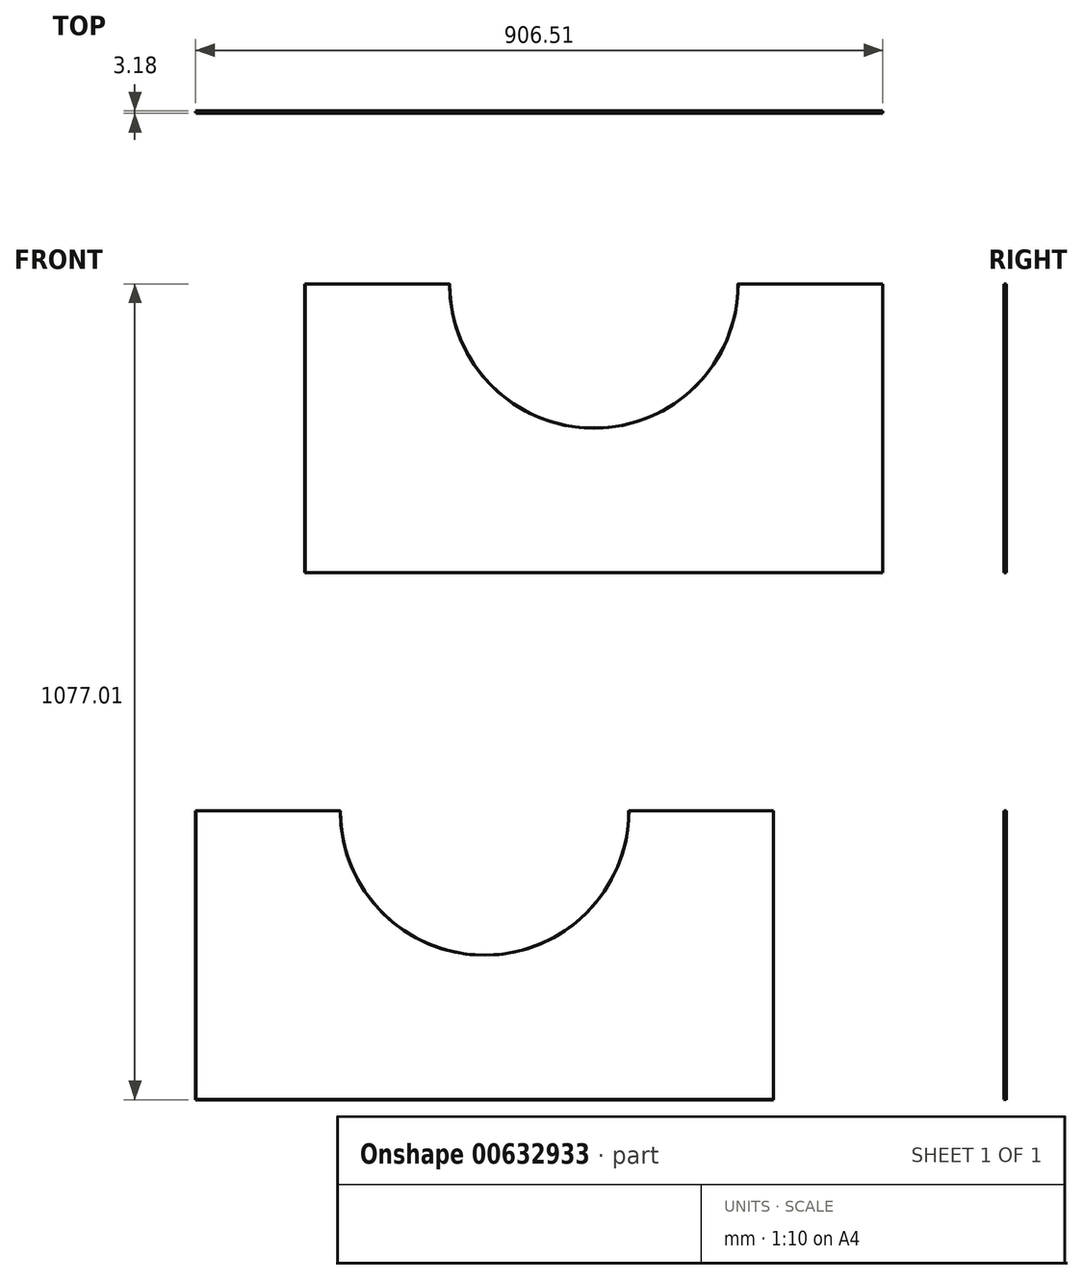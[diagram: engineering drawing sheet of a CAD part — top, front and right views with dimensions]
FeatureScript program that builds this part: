
annotation { "Feature Type Name" : "Feature", "Feature Type Description" : "" }
export const myFeature = defineFeature(function(context is Context, id is Id, definition is map)
    precondition{}
    {
        {
            var Q0;
            Q0=qCreatedBy(makeId("Front.planeOp"),FACE);
            var sketch = newSketch(context, id + "F0", { "sketchPlane" : qUnion([Q0])});
            skLineSegment(sketch, "E0.bottom", {"start": v(-190.5, 0) * mm, "end": v(-381, 0) * mm});
            skLineSegment(sketch, "E0.top", {"start": v(0, -381) * mm, "end": v(-381, -381) * mm});
            skLineSegment(sketch, "E0.right", {"start": v(-381, 0) * mm, "end": v(-381, -381) * mm});
            skPoint(sketch, "E1", {"position": v(-190.5, 0) * mm});
            skArc(sketch, "E2", {"start": v(-190.5, 0) * mm, "mid": v(-134.7, -134.7) * mm, "end": v(0, -190.5) * mm});
            skArc(sketch, "E3.MirrorCS", {"start": v(190.5, 0) * mm, "mid": v(134.7, -134.7) * mm, "end": v(0, -190.5) * mm});
            skLineSegment(sketch, "E4.MirrorCS", {"start": v(190.5, 0) * mm, "end": v(381, 0) * mm});
            skLineSegment(sketch, "E5.MirrorCS", {"start": v(381, 0) * mm, "end": v(381, -381) * mm});
            skLineSegment(sketch, "E6.MirrorCS", {"start": v(0, -381) * mm, "end": v(381, -381) * mm});
            skLineSegment(sketch, "E7.bottom", {"start": v(-46.33, 695.68) * mm, "end": v(-236.83, 695.68) * mm});
            skLineSegment(sketch, "E7.top", {"start": v(144.17, 314.68) * mm, "end": v(-236.83, 314.68) * mm});
            skLineSegment(sketch, "E7.right", {"start": v(-236.83, 695.68) * mm, "end": v(-236.83, 314.68) * mm});
            skPoint(sketch, "E8", {"position": v(-46.33, 695.68) * mm});
            skArc(sketch, "E9", {"start": v(-46.33, 695.68) * mm, "mid": v(9.47, 560.97) * mm, "end": v(144.17, 505.18) * mm});
            skArc(sketch, "E10.MirrorCS", {"start": v(334.67, 695.68) * mm, "mid": v(278.88, 560.97) * mm, "end": v(144.17, 505.18) * mm});
            skLineSegment(sketch, "E11.MirrorCS", {"start": v(334.67, 695.68) * mm, "end": v(525.17, 695.68) * mm});
            skLineSegment(sketch, "E12.MirrorCS", {"start": v(525.17, 695.68) * mm, "end": v(525.17, 314.68) * mm});
            skLineSegment(sketch, "E13.MirrorCS", {"start": v(144.17, 314.68) * mm, "end": v(525.17, 314.68) * mm});
            skSolve(sketch);
        }
        {
            var Q0;
            Q0=makeQuery(id+"F0.imprint","IMPRINT",FACE,{"disambiguationData":[TD([[makeQuery(id+"F0.imprint","IMPRINT",EDGE,{"derivedFrom":sQuery(id+"F0.wireOp",EDGE,"E7.bottom")}),1.0]])]});
            var Q1;
            Q1=makeQuery(id+"F0.imprint","IMPRINT",FACE,{"disambiguationData":[TD([[makeQuery(id+"F0.imprint","IMPRINT",EDGE,{"derivedFrom":sQuery(id+"F0.wireOp",EDGE,"E0.bottom")}),1.0]])]});
            extrude(context, id + "F1", {"entities" : qUnion([Q0, Q1]), "oppositeDirection" : true, "depth" : 3.17 * mm, "offsetDistance" : 25.4 * mm, "hasDraft" : true, "draftAngle" : 3 * degree});
        }
        {
            var Q0;
            Q0=makeQuery(id+"F0.imprint","IMPRINT",FACE,{"disambiguationData":[TD([[makeQuery(id+"F0.imprint","IMPRINT",EDGE,{"derivedFrom":sQuery(id+"F0.wireOp",EDGE,"E0.bottom")}),1.0]])]});
            extrude(context, id + "F2", {"entities" : qUnion([Q0]), "operationType" : NewBodyOperationType.ADD, "oppositeDirection" : true, "depth" : 3.17 * mm, "offsetDistance" : 25.4 * mm});
        }
    });
